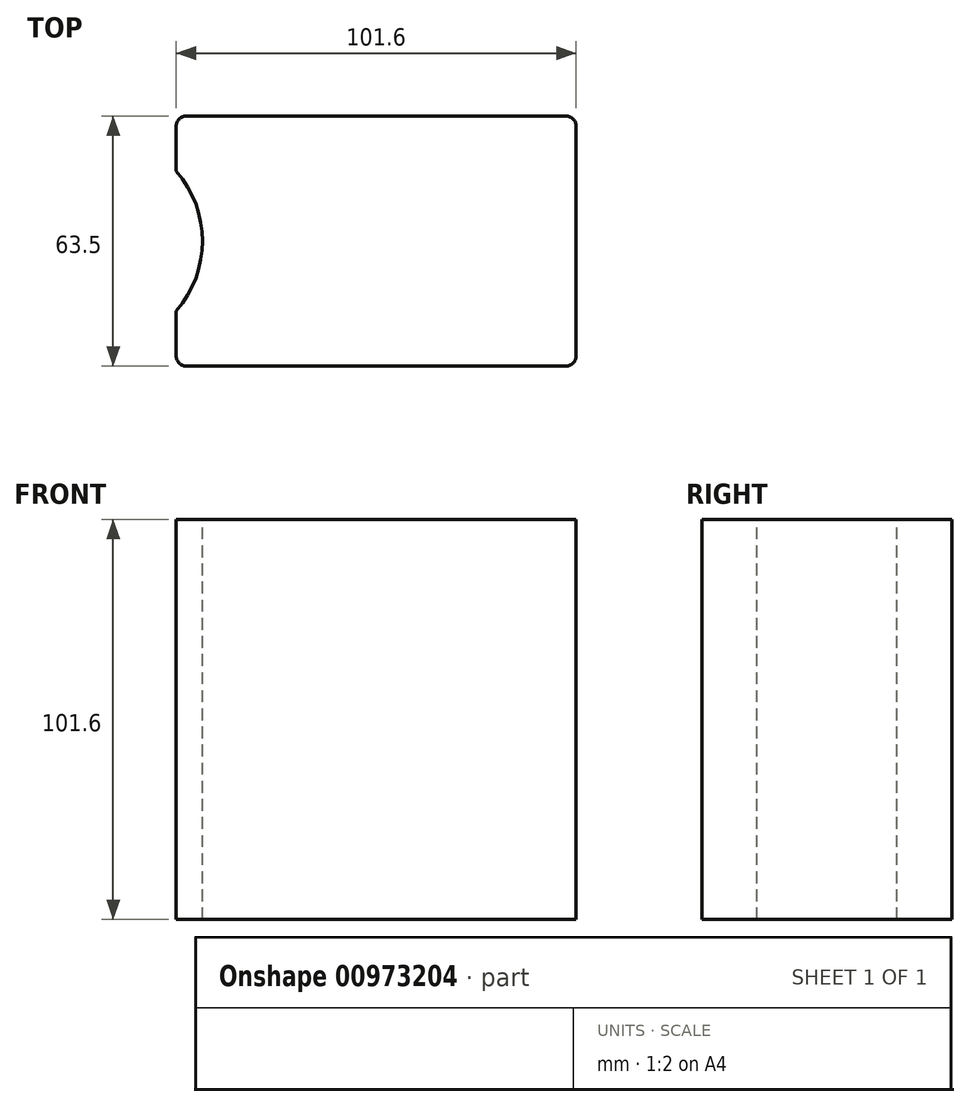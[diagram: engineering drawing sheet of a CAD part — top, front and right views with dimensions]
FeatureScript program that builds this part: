
annotation { "Feature Type Name" : "Feature", "Feature Type Description" : "" }
export const myFeature = defineFeature(function(context is Context, id is Id, definition is map)
    precondition{}
    {
        {
            var Q0;
            Q0=qCreatedBy(makeId("Top.planeOp"),FACE);
            var sketch = newSketch(context, id + "F0", { "sketchPlane" : qUnion([Q0])});
            skLineSegment(sketch, "E0.bottom", {"start": v(48.26, 31.75) * mm, "end": v(-48.26, 31.75) * mm});
            skLineSegment(sketch, "E0.top", {"start": v(48.26, -31.75) * mm, "end": v(-48.26, -31.75) * mm});
            skLineSegment(sketch, "E0.left", {"start": v(50.8, 29.21) * mm, "end": v(50.8, -29.21) * mm});
            skLineSegment(sketch, "E0.right", {"start": v(-50.8, 29.21) * mm, "end": v(-50.8, -29.21) * mm});
            skPoint(sketch, "E0.middle", {"position": v(0, 0) * mm});
            skCircle(sketch, "E1", {"center": v(-71.12, 0) * mm, "radius": 26.99 * mm});
            skPoint(sketch, "E2.visualSharp", {"position": v(50.8, 31.75) * mm});
            skArc(sketch, "E2.filletArc", {"start": v(50.8, 29.21) * mm, "mid": v(50.06, 31) * mm, "end": v(48.26, 31.75) * mm});
            skPoint(sketch, "E3.visualSharp", {"position": v(50.8, -31.75) * mm});
            skArc(sketch, "E3.filletArc", {"start": v(48.26, -31.75) * mm, "mid": v(50.06, -31) * mm, "end": v(50.8, -29.21) * mm});
            skPoint(sketch, "E4.visualSharp", {"position": v(-50.8, -31.75) * mm});
            skArc(sketch, "E4.filletArc", {"start": v(-50.8, -29.21) * mm, "mid": v(-50.06, -31) * mm, "end": v(-48.26, -31.75) * mm});
            skPoint(sketch, "E5.visualSharp", {"position": v(-50.8, 31.75) * mm});
            skArc(sketch, "E5.filletArc", {"start": v(-48.26, 31.75) * mm, "mid": v(-50.06, 31) * mm, "end": v(-50.8, 29.21) * mm});
            skSolve(sketch);
        }
        {
            var Q0;
            {var subQ0=sQuery(id+"F0.wireOp",EDGE,"E1");var subQ1=sQuery(id+"F0.wireOp",EDGE,"E0.right");var subQ2=makeQuery(id+"F0.imprint","INTERSECT",VERTEX,{"disambiguationData":[OD(0.0)],"derivedFrom":[subQ1,subQ0]});Q0=makeQuery(id+"F0.imprint","IMPRINT",FACE,{"disambiguationData":[TD([[makeQuery(id+"F0.imprint","IMPRINT",EDGE,{"disambiguationData":[TD([[subQ2,-1.0]])],"derivedFrom":subQ1}),-1.0]])]});}
            var Q1;
            {var subQ0=sQuery(id+"F0.wireOp",EDGE,"E1");var subQ4=makeQuery(id+"F0.imprint","IMPRINT",VERTEX,{"derivedFrom":subQ0});Q1=makeQuery(id+"F0.imprint","IMPRINT",FACE,{"disambiguationData":[TD([[makeQuery(id+"F0.imprint","IMPRINT",EDGE,{"disambiguationData":[TD([[subQ4,-1.0]])],"derivedFrom":subQ0}),1.0]])]});}
            var Q2;
            Q2=makeQuery(id+"F0.imprint","IMPRINT",FACE,{"disambiguationData":[TD([[makeQuery(id+"F0.imprint","IMPRINT",EDGE,{"derivedFrom":sQuery(id+"F0.wireOp",EDGE,"E0.bottom")}),1.0]])]});
            extrude(context, id + "F1", {"entities" : qUnion([Q0, Q1, Q2]), "oppositeDirection" : true, "depth" : 101.6 * mm, "offsetDistance" : 25.4 * mm});
        }
    });
